# Revit family: Deca_Misturador de parede para lavatório_Dream_1878.87
name_source: partatom
category: Plumbing Fixtures
units: mm (PartAtom-declared; Revit-internal decimal feet)

## family parameters
Cut with Voids When Loaded = No
Host = Face
Part Type = Normal
Room Calculation Point = No
Round Connector Dimension = Use Radius
Shared = No

## types (7) — shared parameters
Acompanha o Produto = Acompanha Deca confort + Válvula de escoamento
Aprovado por = quattroD
Atendimento ao Cliente = 0800-0117073
CW Connection = No
Categoria = METAIS PARA BANHEIRO
Composição Anel Vedação = -
Composição Assento = -
Composição Básica = Liga de Cobre (bronze e latão),Plásticos de Engenharia,Elastômeros
Composição Componente = -
Consumo = -
Cor Interna = -
Cor Secundária = -
Cores Componente = -
Criado por = quattroD
Código Pai = 1878.87
Default Elevation = 1100 mm
Diâmetro Água Fria = 20 mm  [stored 0.0656168 ft]
Diâmetro Água Quente = 20 mm  [stored 0.0656168 ft]
HW Connection = No
Informações Complementares = -
Itens de Instalação = -
Linha = Dream
Manufacturer = Deca
Norma = NBR16749
Pressão máx. funcionamento = 40 MCA
Pressão mín. Aquec. Acúmulo = -
Pressão mín. Aquec. Passagem = -
Pressão mín. funcionamento = 2 MCA
Raio Água Fria = 10 mm  [stored 0.0328084 ft]
Raio Água Quente = 10 mm  [stored 0.0328084 ft]
Saída de Esgoto = -
Segmento = Banheiro Luxo
Tipo de dispositivo economizador = Sim
Tipo de mecanismo utilizado = MVC -1/4 volta
Tipo de rosca de entrada = BSP NBR 8133
Tipo de rosca de saída = -
URL = www.deca.com.br
Vazão na Pressão máx. (L/min) = 6
Vazão na Pressão mín. (L/min) = 4
Vent Connection = No
Waste Connection = No
zero-valued in all types: CWFU, HWFU, WFU

## per-type parameters (varying)
| type | Cor Principal | Description | Material | Model | Peso Líquido (Kg) |
| 1878.C87_Cromado | Cromado | Misturador de parede para lavatório | Deca_Cromado | 1878.C87 | 4.44 |
| 1878.BL87.MT_Black Matte | Black Matte | Misturador de parede para lavatório | Deca_Black Matte | 1878.BL87.MT | 3.62 |
| 1878.BL87.MT.T01_Black Matte | Black Matte | Misturador de parede para lavatório | Deca_Black Matte - Com Textura | 1878.BL87.MT.T01 | 3.275 |
| 1878.CT87.MT_Corten | Corten | Misturador de parede para lavatório | Deca_Corten | 1878.CT87.MT | 3.447 |
| 1878.CT87.MT.T01_Corten | Corten | Misturador de parede com textura para lavatório | Deca_Corten - Com Textura | 1878.CT87.MT.T01 | 3.275 |
| 1878.GL87.MT_Gold Matte | Gold Matte | Misturador de parede para lavatório | Deca_Gold Matte | 1878.GL87.MT | 3.619 |
| 1878.GL87.RD_Red Gold | Red Gold | Misturador de parede para lavatório | Deca_Red Gold | 1878.GL87.RD | 4.449 |

note: source unit labels omitted for Vazão na Pressão máx. (L/min), Vazão na Pressão mín. (L/min) — the stored unit's dimension contradicts the parameter name (converter mislabeling)

note: [stored X ft] marks values corroborated as IEEE doubles in the binary element streams (Revit-internal decimal feet)

## geometry (parser evidence)
native form markers: Sweep x2
no freeform markers — native parametric forms only
